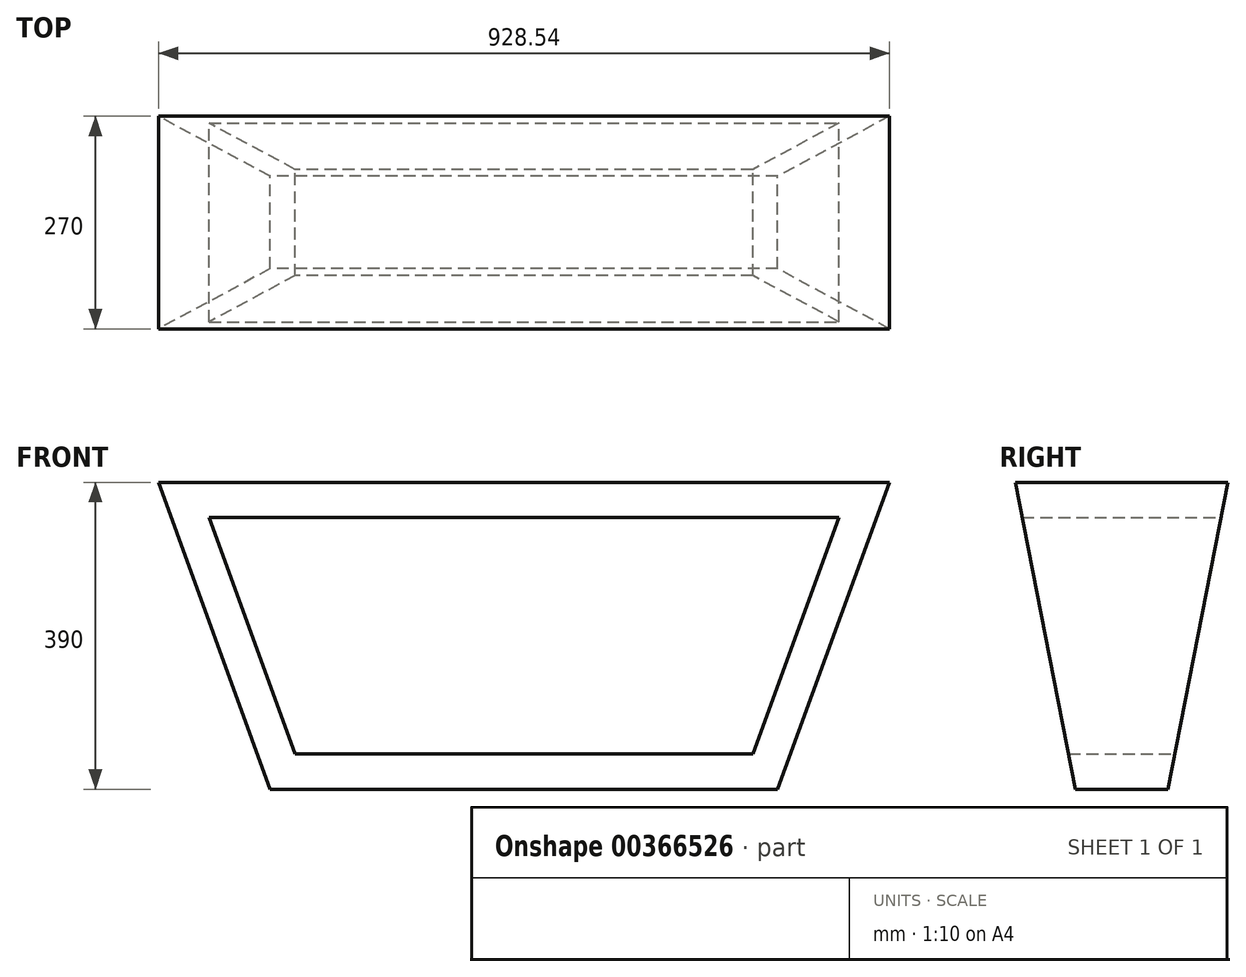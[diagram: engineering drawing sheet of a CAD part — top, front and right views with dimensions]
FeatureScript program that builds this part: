
annotation { "Feature Type Name" : "Feature", "Feature Type Description" : "" }
export const myFeature = defineFeature(function(context is Context, id is Id, definition is map)
    precondition{}
    {
        {
            var Q0;
            Q0=qCreatedBy(makeId("Front.planeOp"),FACE);
            var sketch = newSketch(context, id + "F0", { "sketchPlane" : qUnion([Q0])});
            skLineSegment(sketch, "E0", {"start": v(-290.8, 0) * mm, "end": v(290.8, 0) * mm});
            skLineSegment(sketch, "E1", {"start": v(290.8, 0) * mm, "end": v(400, 300) * mm});
            skLineSegment(sketch, "E2", {"start": v(400, 300) * mm, "end": v(-400, 300) * mm});
            skLineSegment(sketch, "E3", {"start": v(-400, 300) * mm, "end": v(-290.8, 0) * mm});
            skLineSegment(sketch, "E4.0", {"start": v(-464.27, 345) * mm, "end": v(-322.32, -45) * mm});
            skLineSegment(sketch, "E4.1", {"start": v(464.27, 345) * mm, "end": v(-464.27, 345) * mm});
            skLineSegment(sketch, "E4.2", {"start": v(322.32, -45) * mm, "end": v(464.27, 345) * mm});
            skLineSegment(sketch, "E4.3", {"start": v(-322.32, -45) * mm, "end": v(322.32, -45) * mm});
            skSolve(sketch);
        }
        {
            var Q0;
            Q0=makeQuery(id+"F0.imprint","IMPRINT",FACE,{"disambiguationData":[TD([[makeQuery(id+"F0.imprint","IMPRINT",EDGE,{"derivedFrom":sQuery(id+"F0.wireOp",EDGE,"E0")}),-1.0]])]});
            extrude(context, id + "F1", {"entities" : qUnion([Q0]), "endBound" : BoundingType.SYMMETRIC, "depth" : 270 * mm});
        }
        {
            var Q0;
            Q0=qCreatedBy(makeId("Right.planeOp"),FACE);
            var sketch = newSketch(context, id + "F2", { "sketchPlane" : qUnion([Q0])});
            skLineSegment(sketch, "E5", {"start": v(-135, 345) * mm, "end": v(135, 345) * mm});
            skLineSegment(sketch, "E6", {"start": v(-135, 345) * mm, "end": v(-67.5, 0) * mm});
            skLineSegment(sketch, "E7", {"start": v(-67.5, 0) * mm, "end": v(0, 0) * mm, "construction": true});
            skLineSegment(sketch, "E8", {"start": v(135, 345) * mm, "end": v(67.5, 0) * mm});
            skLineSegment(sketch, "E9", {"start": v(0, 0) * mm, "end": v(67.5, 0) * mm, "construction": true});
            skLineSegment(sketch, "E10.2", {"start": v(-274.2, 496.46) * mm, "end": v(427.66, 496.46) * mm});
            skLineSegment(sketch, "E11", {"start": v(-67.5, 0) * mm, "end": v(-57.72, -50) * mm});
            skLineSegment(sketch, "E12", {"start": v(67.5, 0) * mm, "end": v(56.69, -55.27) * mm});
            skLineSegment(sketch, "E13", {"start": v(-57.72, -50) * mm, "end": v(-274.2, -50) * mm});
            skLineSegment(sketch, "E14", {"start": v(-274.2, -50) * mm, "end": v(-274.2, 496.46) * mm});
            skLineSegment(sketch, "E15", {"start": v(56.69, -55.27) * mm, "end": v(427.66, -55.27) * mm});
            skLineSegment(sketch, "E16", {"start": v(427.66, -55.27) * mm, "end": v(427.66, 496.46) * mm});
            skSolve(sketch);
        }
        {
            var Q0;
            Q0=makeQuery(id+"F2.imprint","IMPRINT",FACE,{"disambiguationData":[TD([[makeQuery(id+"F2.imprint","IMPRINT",EDGE,{"derivedFrom":sQuery(id+"F2.wireOp",EDGE,"E5")}),1.0]])]});
            extrude(context, id + "F3", {"entities" : qUnion([Q0]), "operationType" : NewBodyOperationType.REMOVE, "endBound" : BoundingType.SYMMETRIC, "depth" : 1000 * mm});
        }
    });
